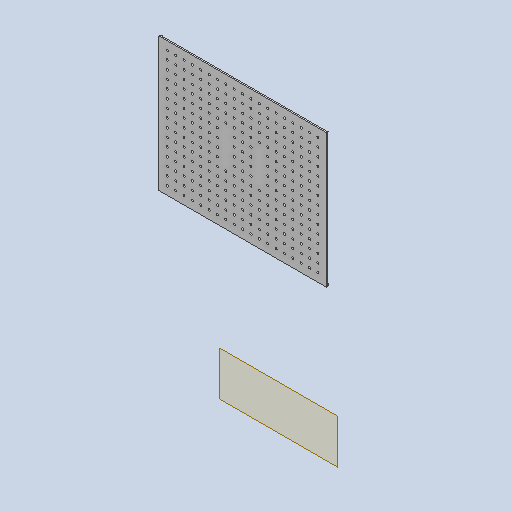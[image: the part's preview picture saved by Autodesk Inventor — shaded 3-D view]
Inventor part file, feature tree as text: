
AUTODESK INVENTOR PART (.ipt)
format: ipt  version: 2024.3 (Build 283343000, 343)  size: 824,320 bytes
history: native  units: in
note: dims shown in document units (in); Inventor stores cm internally (conversion verified against a paired STEP export)
features: other x4, extrude x3, sketch x3, fillet x2, plane x1
ambient origin geometry x8: Origin, YZ Plane, XZ Plane, XY Plane, X Axis, Y Axis, Z Axis, Center Point
bodies: Solid1 (feature_tree)
feature tree (13):
  plane  "Work Plane1"
  extrude  "Extrusion1"  Depth=0.3937in
  extrude  "Extrusion2"  Depth=0.1969in
  extrude  "Extrusion3"  Depth=0.0787in
  fillet  "Fillet2"  Radius=0.126in
  fillet  "Fillet3"  Radius=0.2756in
  sketch  "Sketch1"  dims[d0=0.3937in d1=1.9685in]
  sketch  "Sketch2"  dims[d2=1.1417in d3=0.1969in]
  sketch  "Sketch3"  dims[d4=1.378in d5=0.0in d6=0.126in d7=0.126in d8=0.2756in d9=0.2756in d10=0.8268in d11=0.1969in d12=0.0in d13=0.0in d14=9.8425in d15=7.874in d16=0.1969in d17=0.0in d19=0.126in d20=0.4921in d21=0.4921in d22=7.4803in d24=0.4921in d25=5.9055in d27=0.4921in d30=0.1181in d31=0.0787in]
  other  "<userpath>\Documents\Nauka\Studia\mgr\Semestr_3\Magisterka\uMule\mechanics\uMule-komplet.iam"
  other  "uMule-komplet.iam"
  other  "uMule-power_pack:1"
  other  "uMule-battery_case:1"
